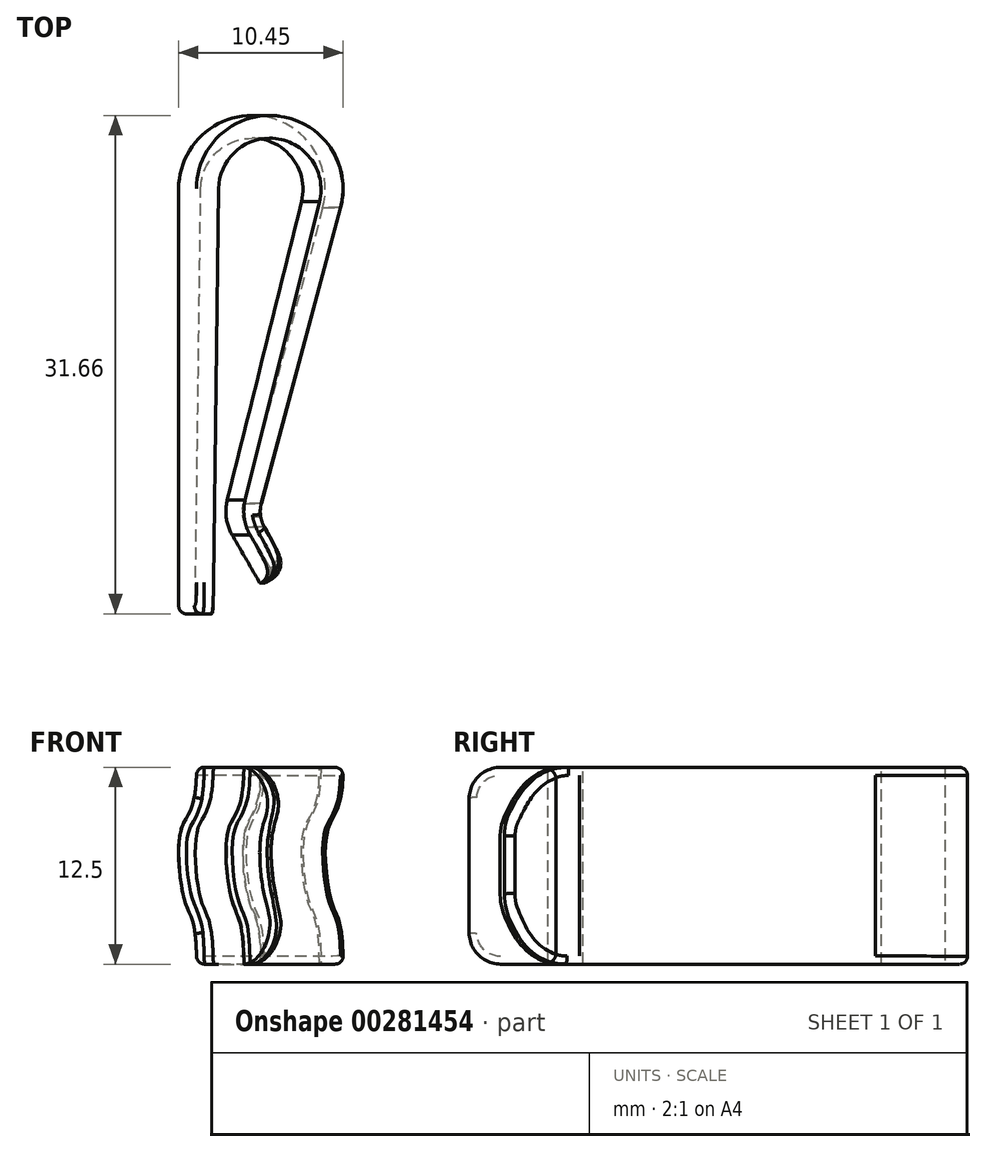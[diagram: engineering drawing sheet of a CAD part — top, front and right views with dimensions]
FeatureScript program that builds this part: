
annotation { "Feature Type Name" : "Feature", "Feature Type Description" : "" }
export const myFeature = defineFeature(function(context is Context, id is Id, definition is map)
    precondition{}
    {
        {
            var Q0;
            Q0=qCreatedBy(makeId("Top.planeOp"),FACE);
            var sketch = newSketch(context, id + "F0", { "sketchPlane" : qUnion([Q0])});
            skLineSegment(sketch, "E0", {"start": v(0, 0) * mm, "end": v(0, 27) * mm});
            skLineSegment(sketch, "E1", {"start": v(3.4, 5) * mm, "end": v(5.15, 1.97) * mm});
            skLineSegment(sketch, "E2", {"start": v(1.05, 0) * mm, "end": v(0, 0) * mm});
            skLineSegment(sketch, "E3", {"start": v(1.4, 27) * mm, "end": v(1.05, 0) * mm});
            skArc(sketch, "E4", {"start": v(0, 27) * mm, "mid": v(5.26, 31.62) * mm, "end": v(9.15, 25.8) * mm});
            skArc(sketch, "E5", {"start": v(1.4, 27) * mm, "mid": v(5.07, 30.18) * mm, "end": v(7.8, 26.17) * mm});
            skLineSegment(sketch, "E6", {"start": v(0, 27) * mm, "end": v(1.4, 27) * mm, "construction": true});
            skArc(sketch, "E7.filletArc", {"start": v(3.09, 7.22) * mm, "mid": v(3.03, 6.08) * mm, "end": v(3.4, 5) * mm});
            skLineSegment(sketch, "E8", {"start": v(5.15, 1.97) * mm, "end": v(6.06, 2.5) * mm});
            skLineSegment(sketch, "E9", {"start": v(6.06, 2.5) * mm, "end": v(4.31, 5.52) * mm});
            skArc(sketch, "E10", {"start": v(4.31, 5.53) * mm, "mid": v(4.07, 6.25) * mm, "end": v(4.12, 7) * mm});
            skLineSegment(sketch, "E11", {"start": v(7.8, 26.17) * mm, "end": v(3.09, 7.22) * mm});
            skLineSegment(sketch, "E12", {"start": v(9.15, 25.8) * mm, "end": v(4.12, 7) * mm});
            skLineSegment(sketch, "E13", {"start": v(7.8, 26.17) * mm, "end": v(9.15, 25.8) * mm, "construction": true});
            skLineSegment(sketch, "E14", {"start": v(3, 8.2) * mm, "end": v(3, 1.87) * mm, "construction": true});
            skSolve(sketch);
        }
        {
            var Q0;
            Q0=qCreatedBy(makeId("Front.planeOp"),FACE);
            var sketch = newSketch(context, id + "F1", { "sketchPlane" : qUnion([Q0])});
            skFitSpline(sketch, "E15", {"points": [v(0, 0) * mm, v(-0.75, 4) * mm, v(-1, 8.5) * mm, v(0, 12.5) * mm], "startDerivative": vector(0, 27.53) * mm, "endDerivative": vector(0, 27.35) * mm});
            skLineSegment(sketch, "E16", {"start": v(-1.14, 1.45) * mm, "end": v(-1.14, 9.55) * mm, "construction": true});
            skSolve(sketch);
        }
        {
            var Q0;
            Q0=qSketchRegion(id+"F0",true);
            var Q1;
            Q1=qConstructionFilter(qBodyType(qCreatedBy(id+"F0",EDGE),BodyType.WIRE),ConstructionObject.NO);
            var Q2;
            Q2=qConstructionFilter(qBodyType(qCreatedBy(id+"F1",EDGE),BodyType.WIRE),ConstructionObject.NO);
            sweep(context, id + "F2", {"profiles" : qUnion([Q0]), "surfaceProfiles" : qUnion([Q1]), "path" : qUnion([Q2]), "keepProfileOrientation" : true});
        }
        {
            var Q0;
            Q0=makeQuery(id+"F2.opSweep","CAP_EDGE",EDGE,{"disambiguationData":[OSD([sQuery(id+"F0.wireOp",EDGE,"E8"),sQuery(id+"F1.wireOp",VERTEX,"E15.end")])],"isStart":false});
            var Q1;
            Q1=makeQuery(id+"F2.opSweep","CAP_EDGE",EDGE,{"disambiguationData":[OSD([sQuery(id+"F0.wireOp",EDGE,"E8"),sQuery(id+"F1.wireOp",VERTEX,"E15.start")])],"isStart":true});
            fillet(context, id + "F3", {"entities" : qUnion([Q0, Q1]), "radius" : 4 * mm, "tangentPropagation" : true, "allowEdgeOverflow" : false});
        }
        {
            var Q0;
            Q0=makeQuery(id+"F2.opSweep","CAP_EDGE",EDGE,{"disambiguationData":[OSD([sQuery(id+"F0.wireOp",EDGE,"E2"),sQuery(id+"F1.wireOp",VERTEX,"E15.end")])],"isStart":false});
            var Q1;
            Q1=makeQuery(id+"F2.opSweep","CAP_EDGE",EDGE,{"disambiguationData":[OSD([sQuery(id+"F0.wireOp",EDGE,"E2"),sQuery(id+"F1.wireOp",VERTEX,"E15.start")])],"isStart":true});
            fillet(context, id + "F4", {"entities" : qUnion([Q0, Q1]), "radius" : 2 * mm, "tangentPropagation" : true, "allowEdgeOverflow" : false});
        }
        {
            var Q0;
            Q0=makeQuery(id+"F3.opFillet","BLEND_EDGE",EDGE,{"blendedFrom":[makeQuery(id+"F2.opSweep","CAP_EDGE",EDGE,{"disambiguationData":[OSD([sQuery(id+"F0.wireOp",EDGE,"E8"),sQuery(id+"F1.wireOp",VERTEX,"E15.end")])],"isStart":false}),makeQuery(id+"F2.opSweep","SWEPT_FACE",FACE,{"disambiguationData":[OSD([sQuery(id+"F0.wireOp",EDGE,"E9"),sQuery(id+"F1.wireOp",EDGE,"E15")])]})],"blendedInto":[makeQuery(id+"F2.opSweep","SWEPT_FACE",FACE,{"disambiguationData":[OSD([sQuery(id+"F0.wireOp",EDGE,"E9"),sQuery(id+"F1.wireOp",EDGE,"E15")])]})]});
            var Q1;
            Q1=makeQuery(id+"F2.opSweep","CAP_EDGE",EDGE,{"disambiguationData":[OSD([sQuery(id+"F0.wireOp",EDGE,"E12"),sQuery(id+"F1.wireOp",VERTEX,"E15.end")])],"isStart":false});
            fillet(context, id + "F5", {"entities" : qUnion([Q0, Q1]), "radius" : 0.5 * mm, "tangentPropagation" : true, "allowEdgeOverflow" : false});
        }
    });
